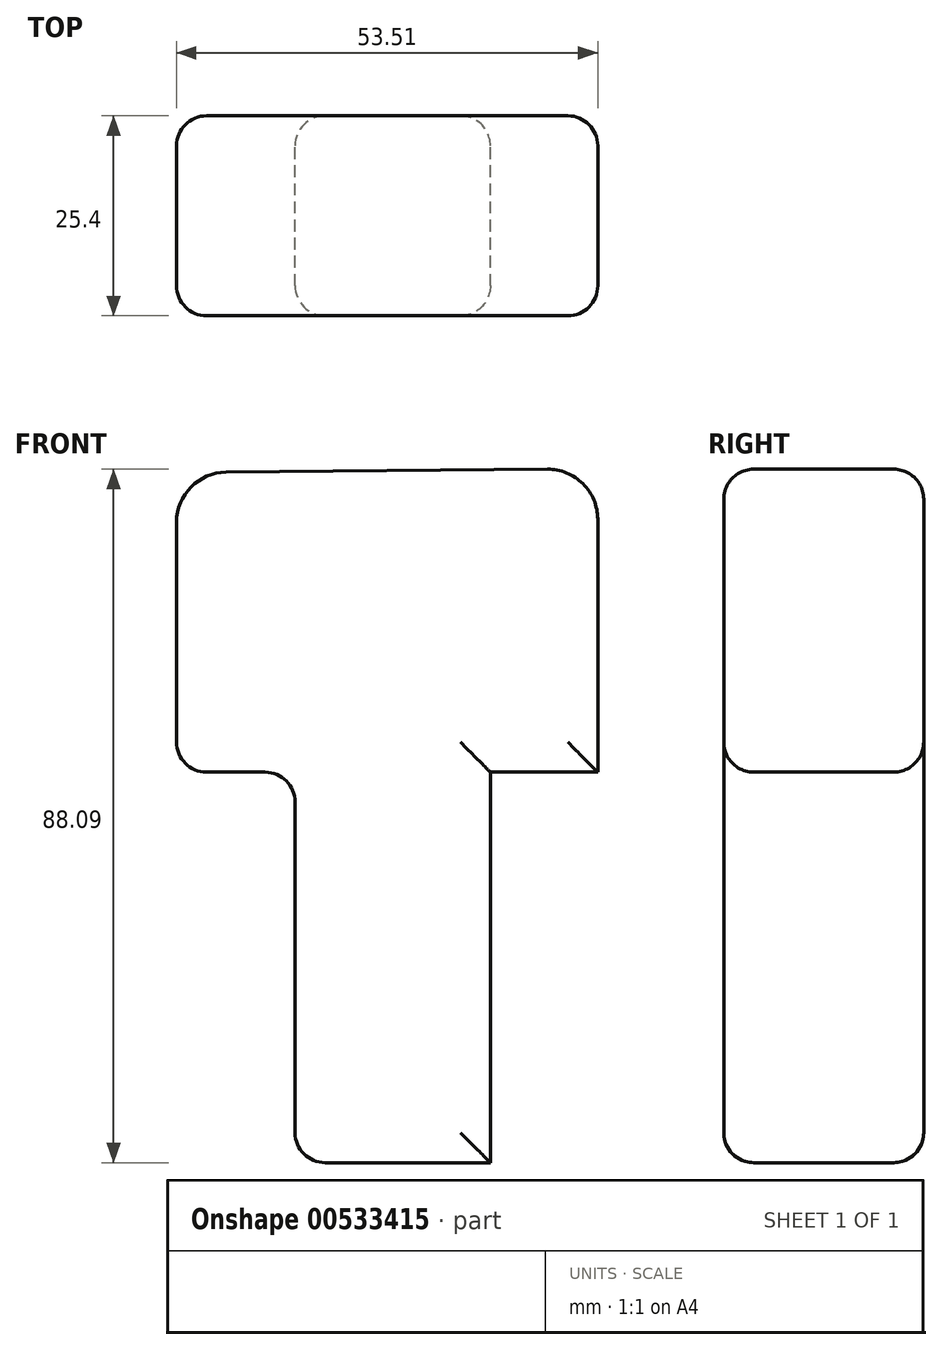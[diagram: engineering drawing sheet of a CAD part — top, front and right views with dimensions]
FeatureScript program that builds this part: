
annotation { "Feature Type Name" : "Feature", "Feature Type Description" : "" }
export const myFeature = defineFeature(function(context is Context, id is Id, definition is map)
    precondition{}
    {
        {
            var Q0;
            Q0=qCreatedBy(makeId("Front.planeOp"),FACE);
            var sketch = newSketch(context, id + "F0", { "sketchPlane" : qUnion([Q0])});
            skLineSegment(sketch, "E0", {"start": v(-14.36, -2.8) * mm, "end": v(-14.36, -52.4) * mm});
            skLineSegment(sketch, "E1", {"start": v(-14.36, -52.4) * mm, "end": v(5.1, -52.4) * mm});
            skLineSegment(sketch, "E2", {"start": v(10.44, -2.8) * mm, "end": v(10.44, -52.4) * mm});
            skLineSegment(sketch, "E3", {"start": v(5.1, -52.4) * mm, "end": v(10.44, -52.4) * mm});
            skLineSegment(sketch, "E4", {"start": v(-14.36, -2.8) * mm, "end": v(-29.43, -2.8) * mm});
            skLineSegment(sketch, "E5", {"start": v(10.44, -2.8) * mm, "end": v(24.08, -2.8) * mm});
            skLineSegment(sketch, "E6", {"start": v(-19.72, -2.8) * mm, "end": v(-24.1, -2.8) * mm});
            skLineSegment(sketch, "E7", {"start": v(-29.43, -2.8) * mm, "end": v(-29.43, 28.97) * mm});
            skLineSegment(sketch, "E8", {"start": v(24.08, -2.8) * mm, "end": v(24.08, 29.34) * mm});
            skLineSegment(sketch, "E9", {"start": v(-23.13, 35.32) * mm, "end": v(17.67, 35.7) * mm});
            skPoint(sketch, "E10.visualSharp", {"position": v(-29.43, 35.26) * mm});
            skArc(sketch, "E10.filletArc", {"start": v(-23.13, 35.32) * mm, "mid": v(-27.59, 33.44) * mm, "end": v(-29.43, 28.97) * mm});
            skPoint(sketch, "E11.visualSharp", {"position": v(24.08, 35.75) * mm});
            skArc(sketch, "E11.filletArc", {"start": v(24.08, 29.34) * mm, "mid": v(22.2, 33.85) * mm, "end": v(17.67, 35.7) * mm});
            skLineSegment(sketch, "E12", {"start": v(-29.43, 0) * mm, "end": v(-29.43, -2.8) * mm});
            skSolve(sketch);
        }
        {
            var Q0;
            Q0 = qSketchRegion(id + "F0", true);
            extrude(context, id + "F1", {"entities" : qUnion([Q0]), "depth" : 25.4 * mm, "offsetDistance" : 25.4 * mm});
        }
        {
            var Q0;
            Q0=makeQuery(id+"F1.opExtrude","CAP_EDGE",EDGE,{"disambiguationData":[OSD([sQuery(id+"F0.wireOp",EDGE,"E4"),sQuery(id+"F0.wireOp",EDGE,"E6")])],"isStart":false});
            var Q1;
            Q1=makeQuery(id+"F1.opExtrude","CAP_EDGE",EDGE,{"disambiguationData":[OSD([sQuery(id+"F0.wireOp",EDGE,"E7"),sQuery(id+"F0.wireOp",EDGE,"E12")])],"isStart":false});
            var Q2;
            Q2=makeQuery(id+"F1.opExtrude","CAP_EDGE",EDGE,{"disambiguationData":[OSD([sQuery(id+"F0.wireOp",EDGE,"E5")])],"isStart":false});
            var Q3;
            Q3=makeQuery(id+"F1.opExtrude","CAP_EDGE",EDGE,{"disambiguationData":[OSD([sQuery(id+"F0.wireOp",EDGE,"E0")])],"isStart":false});
            var Q4;
            Q4=makeQuery(id+"F1.opExtrude","CAP_FACE",FACE,{"disambiguationData":[OSD([sQuery(id+"F0.wireOp",EDGE,"E0"),sQuery(id+"F0.wireOp",EDGE,"E1"),sQuery(id+"F0.wireOp",EDGE,"E2"),sQuery(id+"F0.wireOp",EDGE,"E3"),sQuery(id+"F0.wireOp",EDGE,"E4"),sQuery(id+"F0.wireOp",EDGE,"E5"),sQuery(id+"F0.wireOp",EDGE,"E6"),sQuery(id+"F0.wireOp",EDGE,"E7"),sQuery(id+"F0.wireOp",EDGE,"E8"),sQuery(id+"F0.wireOp",EDGE,"E9"),sQuery(id+"F0.wireOp",EDGE,"E10.filletArc"),sQuery(id+"F0.wireOp",EDGE,"E11.filletArc"),sQuery(id+"F0.wireOp",EDGE,"E12")])],"isStart":false});
            var Q5;
            Q5=makeQuery(id+"F1.opExtrude","SWEPT_EDGE",EDGE,{"disambiguationData":[OSD([sQuery(id+"F0.wireOp",EDGE,"E0"),sQuery(id+"F0.wireOp",EDGE,"E1")])]});
            var Q6;
            Q6=makeQuery(id+"F1.opExtrude","CAP_EDGE",EDGE,{"disambiguationData":[OSD([sQuery(id+"F0.wireOp",EDGE,"E0")])],"isStart":true});
            var Q7;
            Q7=makeQuery(id+"F1.opExtrude","SWEPT_EDGE",EDGE,{"disambiguationData":[OSD([sQuery(id+"F0.wireOp",EDGE,"E4"),sQuery(id+"F0.wireOp",EDGE,"E12")])]});
            var Q8;
            Q8=makeQuery(id+"F1.opExtrude","CAP_EDGE",EDGE,{"disambiguationData":[OSD([sQuery(id+"F0.wireOp",EDGE,"E4"),sQuery(id+"F0.wireOp",EDGE,"E6")])],"isStart":true});
            var Q9;
            Q9=makeQuery(id+"F1.opExtrude","CAP_EDGE",EDGE,{"disambiguationData":[OSD([sQuery(id+"F0.wireOp",EDGE,"E7"),sQuery(id+"F0.wireOp",EDGE,"E12")])],"isStart":true});
            var Q10;
            Q10=makeQuery(id+"F1.opExtrude","CAP_FACE",FACE,{"disambiguationData":[OSD([sQuery(id+"F0.wireOp",EDGE,"E0"),sQuery(id+"F0.wireOp",EDGE,"E1"),sQuery(id+"F0.wireOp",EDGE,"E2"),sQuery(id+"F0.wireOp",EDGE,"E3"),sQuery(id+"F0.wireOp",EDGE,"E4"),sQuery(id+"F0.wireOp",EDGE,"E5"),sQuery(id+"F0.wireOp",EDGE,"E6"),sQuery(id+"F0.wireOp",EDGE,"E7"),sQuery(id+"F0.wireOp",EDGE,"E8"),sQuery(id+"F0.wireOp",EDGE,"E9"),sQuery(id+"F0.wireOp",EDGE,"E10.filletArc"),sQuery(id+"F0.wireOp",EDGE,"E11.filletArc"),sQuery(id+"F0.wireOp",EDGE,"E12")])],"isStart":true});
            fillet(context, id + "F2", {"entities" : qUnion([Q0, Q1, Q2, Q3, Q4, Q5, Q6, Q7, Q8, Q9, Q10]), "radius" : 3.8 * mm, "tangentPropagation" : true, "allowEdgeOverflow" : false});
        }
    });
